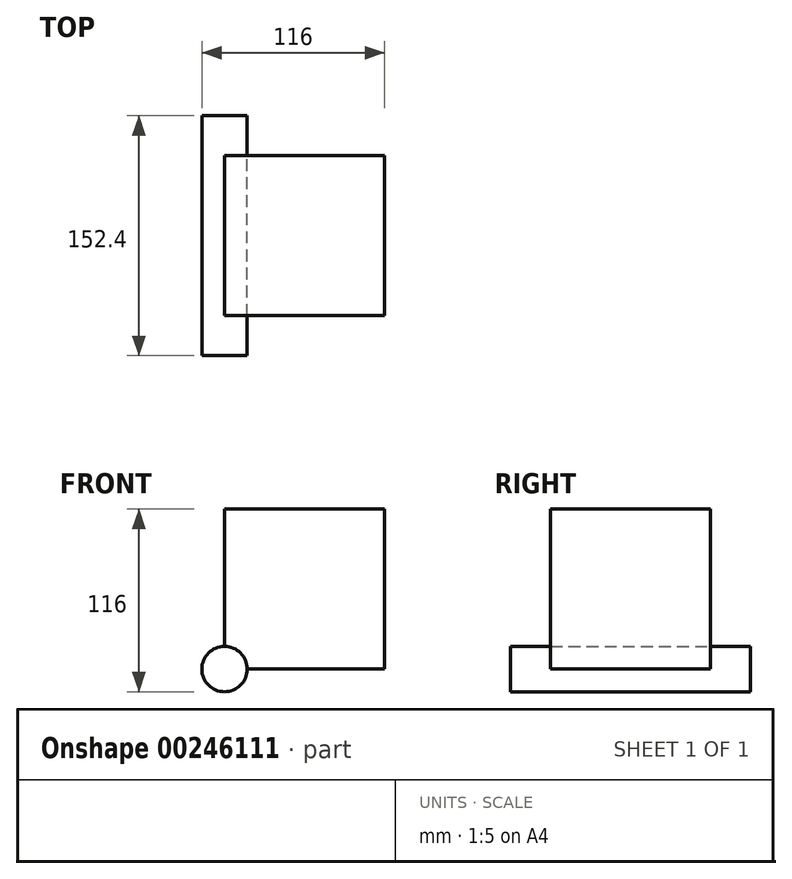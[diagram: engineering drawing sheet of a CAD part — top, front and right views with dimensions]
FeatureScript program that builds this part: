
annotation { "Feature Type Name" : "Feature", "Feature Type Description" : "" }
export const myFeature = defineFeature(function(context is Context, id is Id, definition is map)
    precondition{}
    {
        {
            var Q0;
            Q0=qCreatedBy(makeId("Front.planeOp"),FACE);
            var sketch = newSketch(context, id + "F0", { "sketchPlane" : qUnion([Q0])});
            skLineSegment(sketch, "E0", {"start": v(0, 0) * mm, "end": v(101.6, 0) * mm});
            skLineSegment(sketch, "E1", {"start": v(101.6, 0) * mm, "end": v(101.6, 101.6) * mm});
            skLineSegment(sketch, "E2", {"start": v(101.6, 101.6) * mm, "end": v(0, 101.6) * mm});
            skLineSegment(sketch, "E3", {"start": v(0, 101.6) * mm, "end": v(0, 0) * mm});
            skSolve(sketch);
        }
        {
            var Q0;
            Q0=makeQuery(id+"F0.imprint","IMPRINT",FACE,{"disambiguationData":[TD([[makeQuery(id+"F0.imprint","IMPRINT",EDGE,{"derivedFrom":sQuery(id+"F0.wireOp",EDGE,"E0")}),1.0]])]});
            extrude(context, id + "F1", {"entities" : qUnion([Q0]), "depth" : 101.6 * mm});
        }
        {
            var Q0;
            Q0=qCreatedBy(makeId("Front.planeOp"),FACE);
            cPlane(context, id + "F2", {"entities" : qUnion([Q0]), "cplaneType" : CPlaneType.OFFSET, "offset" : 101.6 * mm, "width" : 152.4 * mm, "height" : 152.4 * mm});
        }
        {
            var Q0;
            Q0=qCreatedBy(id+"F2.planeOp",FACE);
            var sketch = newSketch(context, id + "F3", { "sketchPlane" : qUnion([Q0])});
            skCircle(sketch, "E4", {"center": v(0, 0) * mm, "radius": 14.4 * mm});
            skSolve(sketch);
        }
        {
            var Q0;
            Q0 = qSketchRegion(id + "F3", true);
            extrude(context, id + "F4", {"entities" : qUnion([Q0]), "operationType" : NewBodyOperationType.ADD, "depth" : 25.4 * mm, "hasSecondDirection" : true, "secondDirectionOppositeDirection" : true, "secondDirectionDepth" : 127 * mm});
        }
    });
